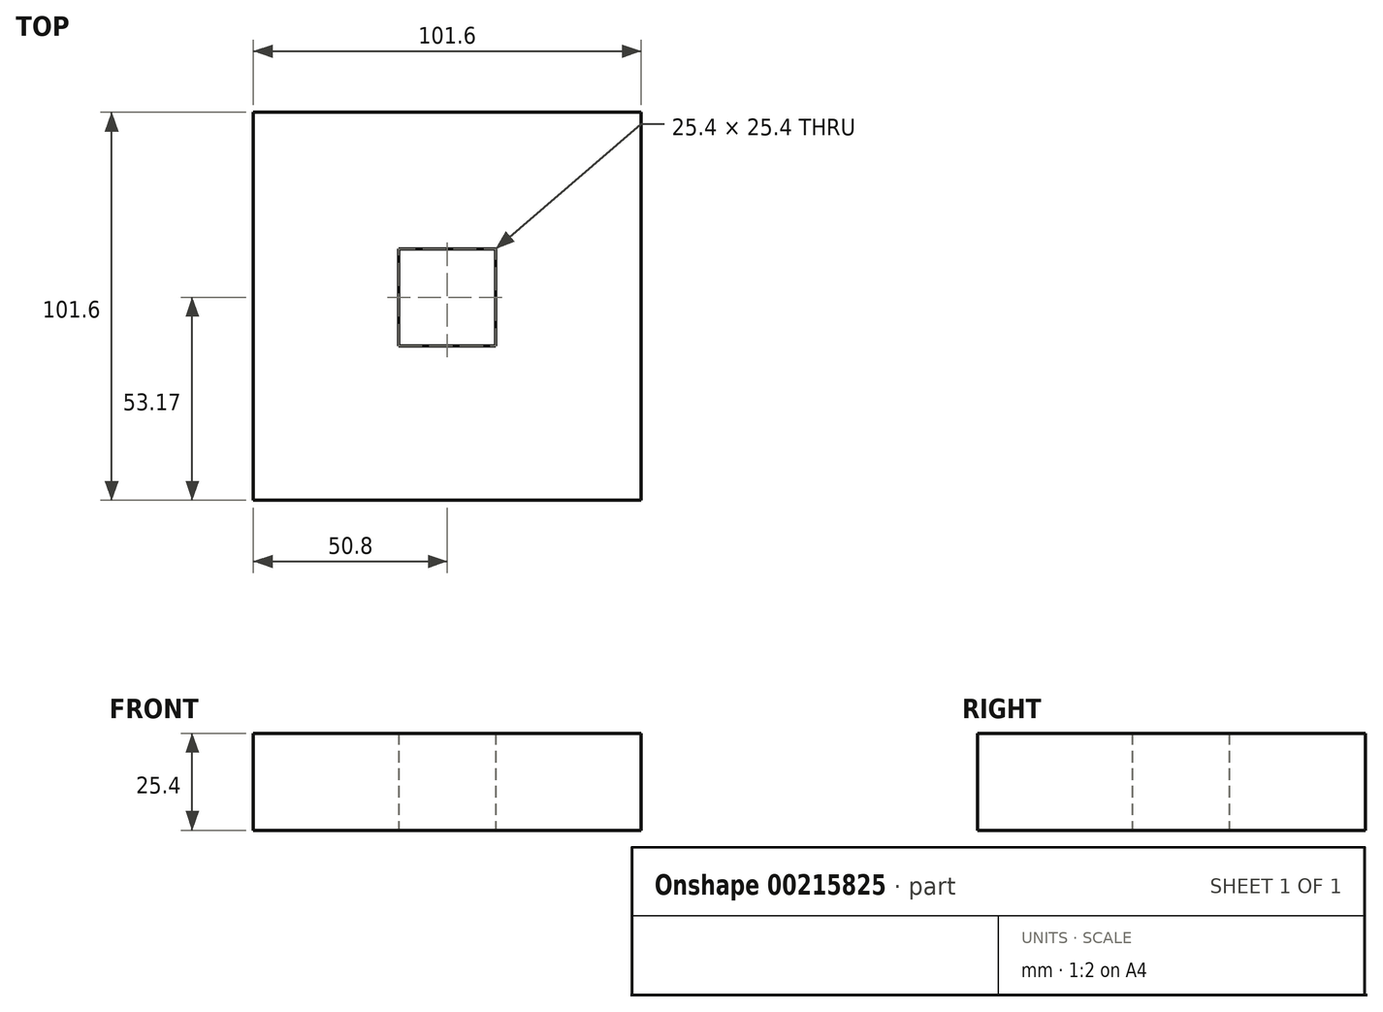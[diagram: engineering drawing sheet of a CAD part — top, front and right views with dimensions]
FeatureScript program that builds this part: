
annotation { "Feature Type Name" : "Feature", "Feature Type Description" : "" }
export const myFeature = defineFeature(function(context is Context, id is Id, definition is map)
    precondition{}
    {
        {
            var Q0;
            Q0=qCreatedBy(makeId("Top.planeOp"),FACE);
            var sketch = newSketch(context, id + "F0", { "sketchPlane" : qUnion([Q0])});
            skLineSegment(sketch, "E0.bottom", {"start": v(-50.8, 48.43) * mm, "end": v(50.8, 48.43) * mm});
            skLineSegment(sketch, "E0.top", {"start": v(-50.8, -53.17) * mm, "end": v(50.8, -53.17) * mm});
            skLineSegment(sketch, "E0.left", {"start": v(-50.8, 48.43) * mm, "end": v(-50.8, -53.17) * mm});
            skLineSegment(sketch, "E0.right", {"start": v(50.8, 48.43) * mm, "end": v(50.8, -53.17) * mm});
            skPoint(sketch, "E0.middle", {"position": v(0, -2.37) * mm});
            skLineSegment(sketch, "E1.bottom", {"start": v(12.7, -12.7) * mm, "end": v(-12.7, -12.7) * mm});
            skLineSegment(sketch, "E1.top", {"start": v(12.7, 12.7) * mm, "end": v(-12.7, 12.7) * mm});
            skLineSegment(sketch, "E1.left", {"start": v(12.7, -12.7) * mm, "end": v(12.7, 12.7) * mm});
            skLineSegment(sketch, "E1.right", {"start": v(-12.7, -12.7) * mm, "end": v(-12.7, 12.7) * mm});
            skPoint(sketch, "E1.middle", {"position": v(0, 0) * mm});
            skSolve(sketch);
        }
        {
            var Q0;
            Q0 = qSketchRegion(id + "F0", true);
            extrude(context, id + "F1", {"entities" : qUnion([Q0]), "depth" : 25.4 * mm});
        }
    });
